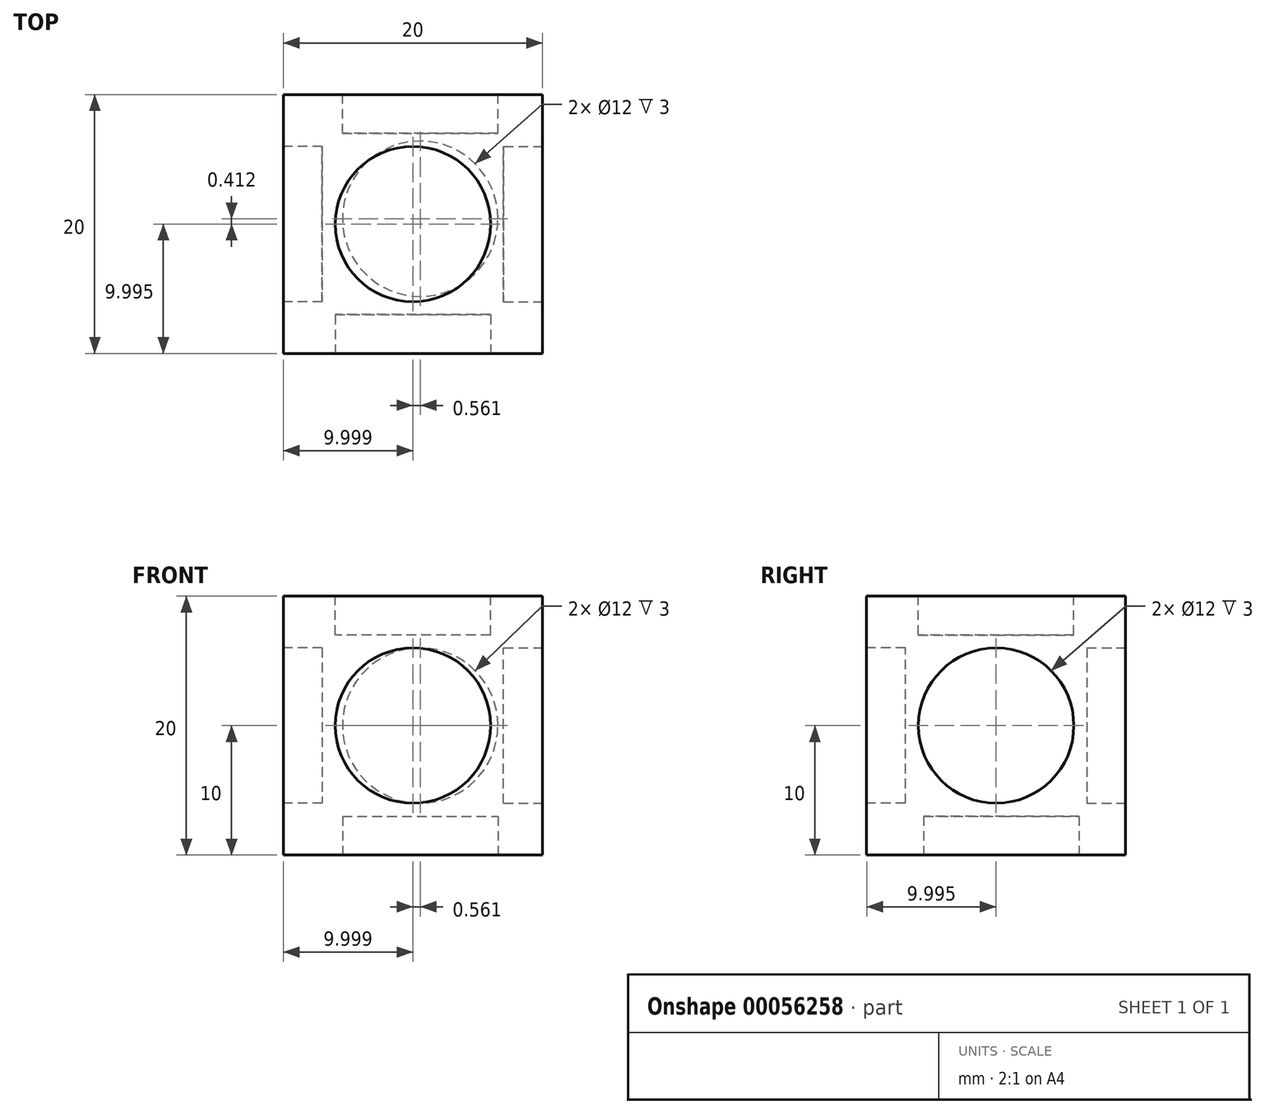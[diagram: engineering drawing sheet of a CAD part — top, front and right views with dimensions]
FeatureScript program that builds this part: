
annotation { "Feature Type Name" : "Feature", "Feature Type Description" : "" }
export const myFeature = defineFeature(function(context is Context, id is Id, definition is map)
    precondition{}
    {
        {
            var Q0;
            Q0=qCreatedBy(makeId("Top.planeOp"),FACE);
            var sketch = newSketch(context, id + "F0", { "sketchPlane" : qUnion([Q0])});
            skLineSegment(sketch, "E0.bottom", {"start": v(-10.56, 8.5) * mm, "end": v(9.44, 8.5) * mm});
            skLineSegment(sketch, "E0.top", {"start": v(-10.56, -11.5) * mm, "end": v(9.44, -11.5) * mm});
            skLineSegment(sketch, "E0.left", {"start": v(-10.56, 8.5) * mm, "end": v(-10.56, -11.5) * mm});
            skLineSegment(sketch, "E0.right", {"start": v(9.44, 8.5) * mm, "end": v(9.44, -11.5) * mm});
            skSolve(sketch);
        }
        {
            var Q0;
            Q0=qSketchRegion(id+"F0",true);
            extrude(context, id + "F1", {"entities" : qUnion([Q0]), "depth" : 20 * mm});
        }
        {
            var Q0;
            Q0=makeQuery(id+"F1.opExtrude","CAP_FACE",FACE,{"disambiguationData":[OSD([sQuery(id+"F0.wireOp",EDGE,"E0.bottom"),sQuery(id+"F0.wireOp",EDGE,"E0.top"),sQuery(id+"F0.wireOp",EDGE,"E0.left"),sQuery(id+"F0.wireOp",EDGE,"E0.right")])],"isStart":false});
            var sketch = newSketch(context, id + "F2", { "sketchPlane" : qUnion([Q0])});
            skCircle(sketch, "E1", {"center": v(-0.56, -1.5) * mm, "radius": 6 * mm});
            skPoint(sketch, "E1.centerSnap0", {"position": v(9.44, -1.5) * mm});
            skPoint(sketch, "E1.centerSnap1", {"position": v(-0.56, 8.5) * mm});
            skSolve(sketch);
        }
        {
            var Q0;
            Q0=qSketchRegion(id+"F2",true);
            extrude(context, id + "F3", {"entities" : qUnion([Q0]), "operationType" : NewBodyOperationType.REMOVE, "oppositeDirection" : true, "depth" : 3 * mm});
        }
        {
            var Q0;
            Q0=makeQuery(id+"F1.opExtrude","SWEPT_FACE",FACE,{"disambiguationData":[OSD([sQuery(id+"F0.wireOp",EDGE,"E0.top")])]});
            var sketch = newSketch(context, id + "F4", { "sketchPlane" : qUnion([Q0])});
            skCircle(sketch, "E2", {"center": v(-0.56, 10) * mm, "radius": 6 * mm});
            skPoint(sketch, "E2.centerSnap0", {"position": v(9.44, 10) * mm});
            skPoint(sketch, "E2.centerSnap1", {"position": v(-0.56, 20) * mm});
            skSolve(sketch);
        }
        {
            var Q0;
            Q0=qSketchRegion(id+"F4",true);
            extrude(context, id + "F5", {"entities" : qUnion([Q0]), "operationType" : NewBodyOperationType.REMOVE, "oppositeDirection" : true, "depth" : 3 * mm});
        }
        {
            var Q0;
            Q0=makeQuery(id+"F1.opExtrude","SWEPT_FACE",FACE,{"disambiguationData":[OSD([sQuery(id+"F0.wireOp",EDGE,"E0.right")])]});
            var sketch = newSketch(context, id + "F6", { "sketchPlane" : qUnion([Q0])});
            skCircle(sketch, "E3", {"center": v(-1.5, 10) * mm, "radius": 6 * mm});
            skPoint(sketch, "E3.centerSnap0", {"position": v(8.5, 10) * mm});
            skPoint(sketch, "E3.centerSnap1", {"position": v(-1.5, 20) * mm});
            skSolve(sketch);
        }
        {
            var Q0;
            Q0=qSketchRegion(id+"F6",true);
            extrude(context, id + "F7", {"entities" : qUnion([Q0]), "operationType" : NewBodyOperationType.REMOVE, "oppositeDirection" : true, "depth" : 3 * mm});
        }
        {
            var Q0;
            Q0=makeQuery(id+"F1.opExtrude","SWEPT_FACE",FACE,{"disambiguationData":[OSD([sQuery(id+"F0.wireOp",EDGE,"E0.left")])]});
            var sketch = newSketch(context, id + "F8", { "sketchPlane" : qUnion([Q0])});
            skCircle(sketch, "E4", {"center": v(1.5, 10) * mm, "radius": 6 * mm});
            skPoint(sketch, "E4.centerSnap0", {"position": v(11.5, 10) * mm});
            skPoint(sketch, "E4.centerSnap1", {"position": v(1.5, 20) * mm});
            skSolve(sketch);
        }
        {
            var Q0;
            Q0=qSketchRegion(id+"F8",true);
            extrude(context, id + "F9", {"entities" : qUnion([Q0]), "operationType" : NewBodyOperationType.REMOVE, "oppositeDirection" : true, "depth" : 3 * mm});
        }
        {
            var Q0;
            Q0=makeQuery(id+"F1.opExtrude","SWEPT_FACE",FACE,{"disambiguationData":[OSD([sQuery(id+"F0.wireOp",EDGE,"E0.bottom")])]});
            var sketch = newSketch(context, id + "F10", { "sketchPlane" : qUnion([Q0])});
            skCircle(sketch, "E5", {"center": v(0, 10) * mm, "radius": 6 * mm});
            skPoint(sketch, "E5.centerSnap0", {"position": v(10.56, 10) * mm});
            skSolve(sketch);
        }
        {
            var Q0;
            Q0=qSketchRegion(id+"F10",true);
            extrude(context, id + "F11", {"entities" : qUnion([Q0]), "operationType" : NewBodyOperationType.REMOVE, "oppositeDirection" : true, "depth" : 3 * mm});
        }
        {
            var Q0;
            Q0=makeQuery(id+"F1.opExtrude","CAP_FACE",FACE,{"disambiguationData":[OSD([sQuery(id+"F0.wireOp",EDGE,"E0.bottom"),sQuery(id+"F0.wireOp",EDGE,"E0.top"),sQuery(id+"F0.wireOp",EDGE,"E0.left"),sQuery(id+"F0.wireOp",EDGE,"E0.right")])],"isStart":true});
            var sketch = newSketch(context, id + "F12", { "sketchPlane" : qUnion([Q0])});
            skCircle(sketch, "E6", {"center": v(0, 1.1) * mm, "radius": 6 * mm});
            skSolve(sketch);
        }
        {
            var Q0;
            Q0=qSketchRegion(id+"F12",true);
            extrude(context, id + "F13", {"entities" : qUnion([Q0]), "operationType" : NewBodyOperationType.REMOVE, "oppositeDirection" : true, "depth" : 3 * mm});
        }
    });
